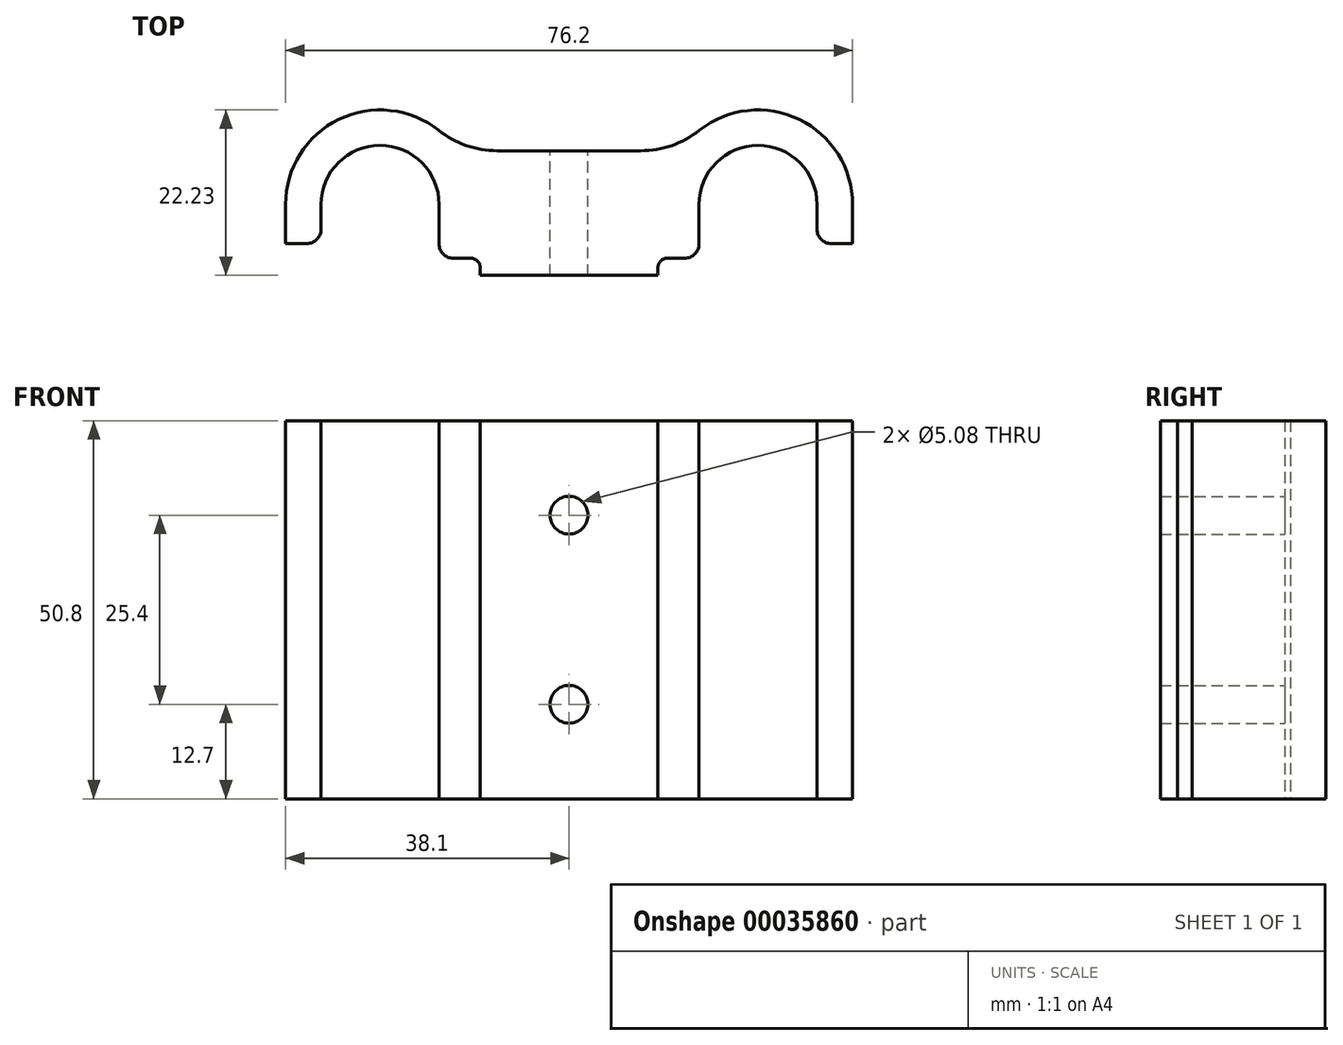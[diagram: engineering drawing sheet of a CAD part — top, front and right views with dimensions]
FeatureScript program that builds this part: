
annotation { "Feature Type Name" : "Feature", "Feature Type Description" : "" }
export const myFeature = defineFeature(function(context is Context, id is Id, definition is map)
    precondition{}
    {
        {
            var Q0;
            Q0=qCreatedBy(makeId("Top.planeOp"),FACE);
            var sketch = newSketch(context, id + "F0", { "sketchPlane" : qUnion([Q0])});
            skArc(sketch, "E0", {"start": v(38.1, 0) * mm, "mid": v(30.93, 11.43) * mm, "end": v(17.52, 9.96) * mm});
            skLineSegment(sketch, "E1.bottom", {"start": v(0, 7.22) * mm, "end": v(9.64, 7.22) * mm});
            skLineSegment(sketch, "E1.top", {"start": v(13.2, -7.22) * mm, "end": v(14.95, -7.22) * mm});
            skLineSegment(sketch, "E1.left", {"start": v(0, 7.22) * mm, "end": v(0, -9.53) * mm});
            skLineSegment(sketch, "E2.top", {"start": v(0, -9.53) * mm, "end": v(11.94, -9.53) * mm});
            skLineSegment(sketch, "E2.right", {"start": v(11.94, -8.5) * mm, "end": v(11.94, -9.53) * mm});
            skArc(sketch, "E3.0", {"start": v(33.34, 0) * mm, "mid": v(25.4, 7.94) * mm, "end": v(17.46, 0) * mm});
            skLineSegment(sketch, "E4", {"start": v(17.46, 0) * mm, "end": v(17.46, -5.32) * mm});
            skLineSegment(sketch, "E5", {"start": v(14.95, -7.22) * mm, "end": v(15.56, -7.22) * mm});
            skLineSegment(sketch, "E6", {"start": v(33.34, 0) * mm, "end": v(33.34, -3.34) * mm});
            skLineSegment(sketch, "E7", {"start": v(35.24, -5.25) * mm, "end": v(38.1, -5.25) * mm});
            skLineSegment(sketch, "E8", {"start": v(38.1, 0) * mm, "end": v(38.1, -5.25) * mm});
            skArc(sketch, "E9.filletArc", {"start": v(13.2, -7.22) * mm, "mid": v(12.31, -7.6) * mm, "end": v(11.94, -8.5) * mm});
            skPoint(sketch, "E10.visualSharp", {"position": v(17.46, -7.22) * mm});
            skArc(sketch, "E10.filletArc", {"start": v(15.56, -7.22) * mm, "mid": v(16.9, -6.66) * mm, "end": v(17.46, -5.32) * mm});
            skPoint(sketch, "E11.visualSharp", {"position": v(33.34, -5.25) * mm});
            skArc(sketch, "E11.filletArc", {"start": v(33.34, -3.34) * mm, "mid": v(33.9, -4.69) * mm, "end": v(35.24, -5.25) * mm});
            skPoint(sketch, "E12.visualSharp", {"position": v(14.95, 7.22) * mm});
            skArc(sketch, "E12.filletArc", {"start": v(9.64, 7.22) * mm, "mid": v(13.81, 7.92) * mm, "end": v(17.52, 9.96) * mm});
            skLineSegment(sketch, "E13.MirrorCS", {"start": v(0, 7.22) * mm, "end": v(-9.64, 7.22) * mm});
            skArc(sketch, "E14.MirrorCS", {"start": v(-9.64, 7.22) * mm, "mid": v(-13.81, 7.92) * mm, "end": v(-17.52, 9.96) * mm});
            skArc(sketch, "E15.MirrorCS", {"start": v(-38.1, 0) * mm, "mid": v(-30.93, 11.43) * mm, "end": v(-17.52, 9.96) * mm});
            skLineSegment(sketch, "E16.MirrorCS", {"start": v(-38.1, 0) * mm, "end": v(-38.1, -5.25) * mm});
            skLineSegment(sketch, "E17.MirrorCS", {"start": v(-35.24, -5.25) * mm, "end": v(-38.1, -5.25) * mm});
            skArc(sketch, "E18.MirrorCS", {"start": v(-33.34, -3.34) * mm, "mid": v(-33.9, -4.69) * mm, "end": v(-35.24, -5.25) * mm});
            skLineSegment(sketch, "E19.MirrorCS", {"start": v(-33.34, 0) * mm, "end": v(-33.34, -3.34) * mm});
            skArc(sketch, "E20.MirrorCS", {"start": v(-33.34, 0) * mm, "mid": v(-25.4, 7.94) * mm, "end": v(-17.46, 0) * mm});
            skLineSegment(sketch, "E21.MirrorCS", {"start": v(-17.46, 0) * mm, "end": v(-17.46, -5.32) * mm});
            skArc(sketch, "E22.MirrorCS", {"start": v(-15.56, -7.22) * mm, "mid": v(-16.9, -6.66) * mm, "end": v(-17.46, -5.32) * mm});
            skLineSegment(sketch, "E23.MirrorCS", {"start": v(-14.95, -7.22) * mm, "end": v(-15.56, -7.22) * mm});
            skLineSegment(sketch, "E24.MirrorCS", {"start": v(-13.2, -7.22) * mm, "end": v(-14.95, -7.22) * mm});
            skArc(sketch, "E25.MirrorCS", {"start": v(-13.2, -7.22) * mm, "mid": v(-12.31, -7.6) * mm, "end": v(-11.94, -8.5) * mm});
            skLineSegment(sketch, "E26.MirrorCS", {"start": v(-11.94, -8.5) * mm, "end": v(-11.94, -9.53) * mm});
            skLineSegment(sketch, "E27.MirrorCS", {"start": v(0, -9.53) * mm, "end": v(-11.94, -9.53) * mm});
            skSolve(sketch);
        }
        {
            var Q0;
            Q0 = qSketchRegion(id + "F0", true);
            extrude(context, id + "F1", {"entities" : qUnion([Q0]), "depth" : 50.8 * mm});
        }
        {
            var Q0;
            Q0=makeQuery(id+"F1.opExtrude","SWEPT_FACE",FACE,{"disambiguationData":[OSD([sQuery(id+"F0.wireOp",EDGE,"E1.bottom"),sQuery(id+"F0.wireOp",EDGE,"E13.MirrorCS")])]});
            var sketch = newSketch(context, id + "F2", { "sketchPlane" : qUnion([Q0])});
            skCircle(sketch, "E28", {"center": v(0, 12.7) * mm, "radius": 2.54 * mm});
            skCircle(sketch, "E29", {"center": v(0, 38.1) * mm, "radius": 2.54 * mm});
            skSolve(sketch);
        }
        {
            var Q0;
            Q0 = qSketchRegion(id + "F2", true);
            extrude(context, id + "F3", {"entities" : qUnion([Q0]), "operationType" : NewBodyOperationType.REMOVE, "endBound" : BoundingType.THROUGH_ALL, "oppositeDirection" : true, "depth" : 25.4 * mm});
        }
    });
